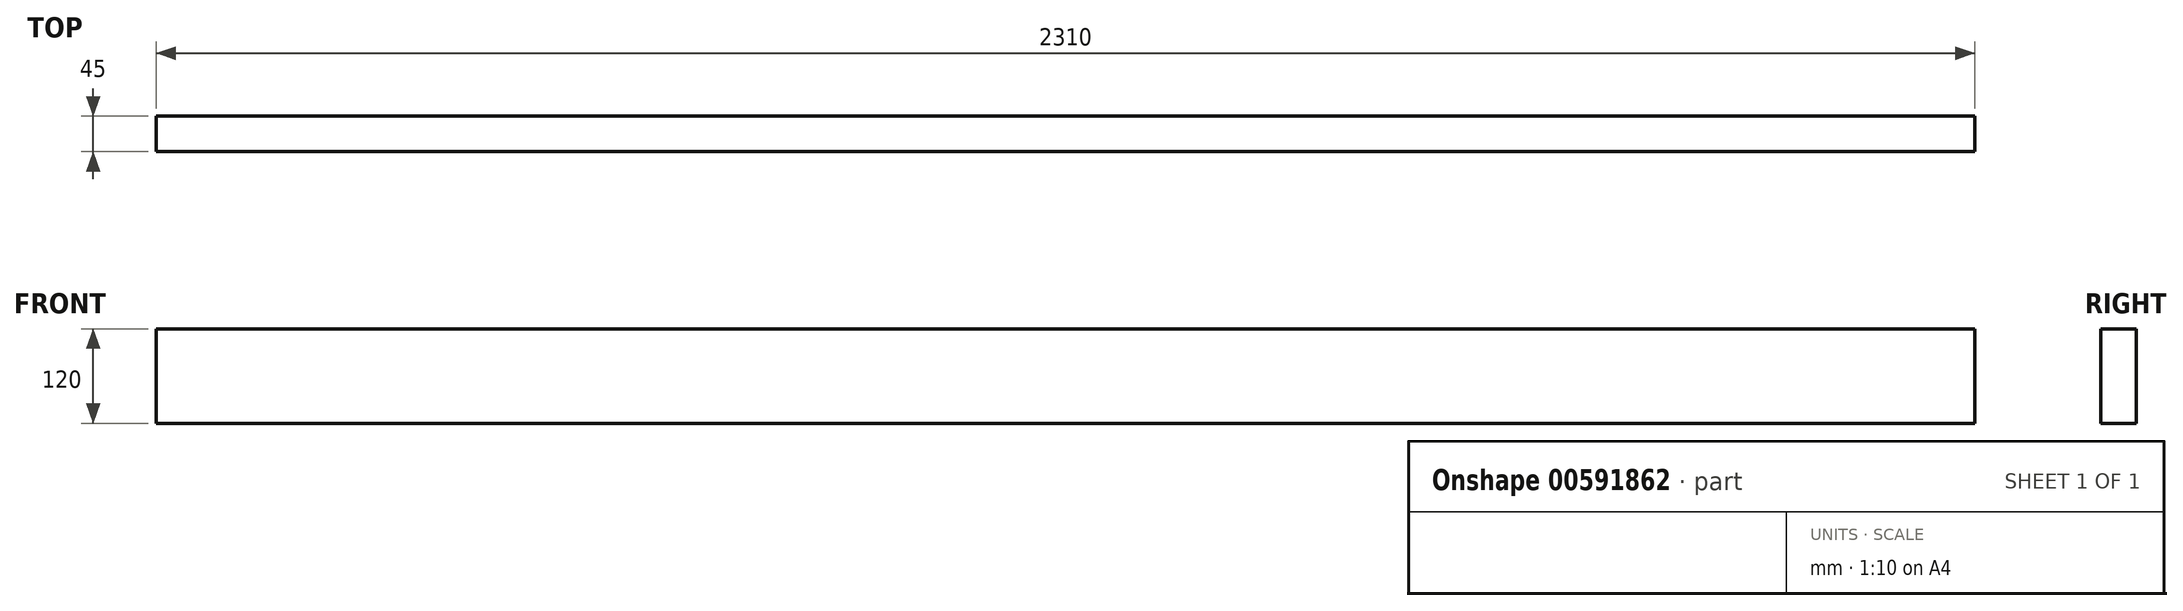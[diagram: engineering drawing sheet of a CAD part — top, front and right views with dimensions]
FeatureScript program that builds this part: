
annotation { "Feature Type Name" : "Feature", "Feature Type Description" : "" }
export const myFeature = defineFeature(function(context is Context, id is Id, definition is map)
    precondition{}
    {
        {
            var Q0;
            Q0=qCreatedBy(makeId("Front.planeOp"),FACE);
            var sketch = newSketch(context, id + "F0", { "sketchPlane" : qUnion([Q0])});
            skLineSegment(sketch, "E0.bottom", {"start": v(0, 0) * mm, "end": v(2310, 0) * mm});
            skLineSegment(sketch, "E0.top", {"start": v(0, 120) * mm, "end": v(2310, 120) * mm});
            skLineSegment(sketch, "E0.left", {"start": v(0, 0) * mm, "end": v(0, 120) * mm});
            skLineSegment(sketch, "E0.right", {"start": v(2310, 0) * mm, "end": v(2310, 120) * mm});
            skSolve(sketch);
        }
        {
            var Q0;
            Q0=makeQuery(id+"F0.imprint","IMPRINT",FACE,{"disambiguationData":[TD([[makeQuery(id+"F0.imprint","IMPRINT",EDGE,{"derivedFrom":sQuery(id+"F0.wireOp",EDGE,"E0.bottom")}),1.0]])]});
            extrude(context, id + "F1", {"entities" : qUnion([Q0]), "depth" : 45 * mm, "offsetDistance" : 25 * mm});
        }
    });
